# Revit family: P560265-020
name_source: partatom
category: Lighting Fixtures
units: mm (PartAtom-declared; Revit-internal decimal feet)

## family parameters
Cut with Voids When Loaded = No
Host = Face
Light Source = No
OmniClass Number = 23.80.70.11.14.17
OmniClass Title = Direct/Indirect
Part Type = Normal
Room Calculation Point = No
Round Connector Dimension = Use Diameter
Shared = Yes

## types (1)
- P560265-020
    Apparent Load = 100 VA
    Assembly Code = D5020200
    Connector Description = Lighting Connector
    Default Elevation = 48 "
    Description = Williamston Collection 1-Light Clear Glass Antique Bronze Farmhouse Outdoor Medium Wall Lantern Light
    Features = Application: Ideal for any porch, patio, deck, garage, barn, entryway, foyer, or bedroom.
Style: Perfect for farmhouse, traditional, and transitional style settings.
Finish: The elongated frame, curved handle, and square backplate are coated in an antique bronze finish for a timeless design with a touch of farmhouse flair.
Materials: Constructed from aluminum to ensure a long product lifespan.
Glass/Shade: A light source glows from within clear glass panes beneath a traditional windowpane design for a classic character.
Bulbs: For ideal illumination, use 1 medium base bulb that is sold separately (100w max - LED/CFL/incandescent). Compatible with dimmable bulbs.
Dimensions: Measures 6-inch length by 14.25-inch height by 7-inch depth (installed).
Certifications: cCSAus wet location listed.
Pairs With: Pairs with a variety of other Progress Lighting fixtures.
Warranty: Our 1-Year Limited Warranty guarantees your complete satisfaction with your purchase and includes professional after-sales customer service support. Make your purchase today to breathe new life into your lighting design!
    Fixture distribution = Direct
    Glass = Hubbell - White Glass
    Gold = Hubbell - Gold
    Housing Material = Paint - Hubbell - Textured Camera Black
    Lamp = LED
    Load Classification = Lighting
    Manufacturer = Progress Lighting
    Model = P560265-020
    Power Factor = 1
    Product Documentation Link = https://hubbellcdn.com
    Product Link = https://www.hubbell.com
    URL = https://www.hubbell.com
    Voltage = 120 V
    Warranty = 1 years Warranty
    Wattage Comments = 100W
    Watts = 100 W

## geometry (parser evidence)
native form markers: Sweep x10
no freeform markers — native parametric forms only
